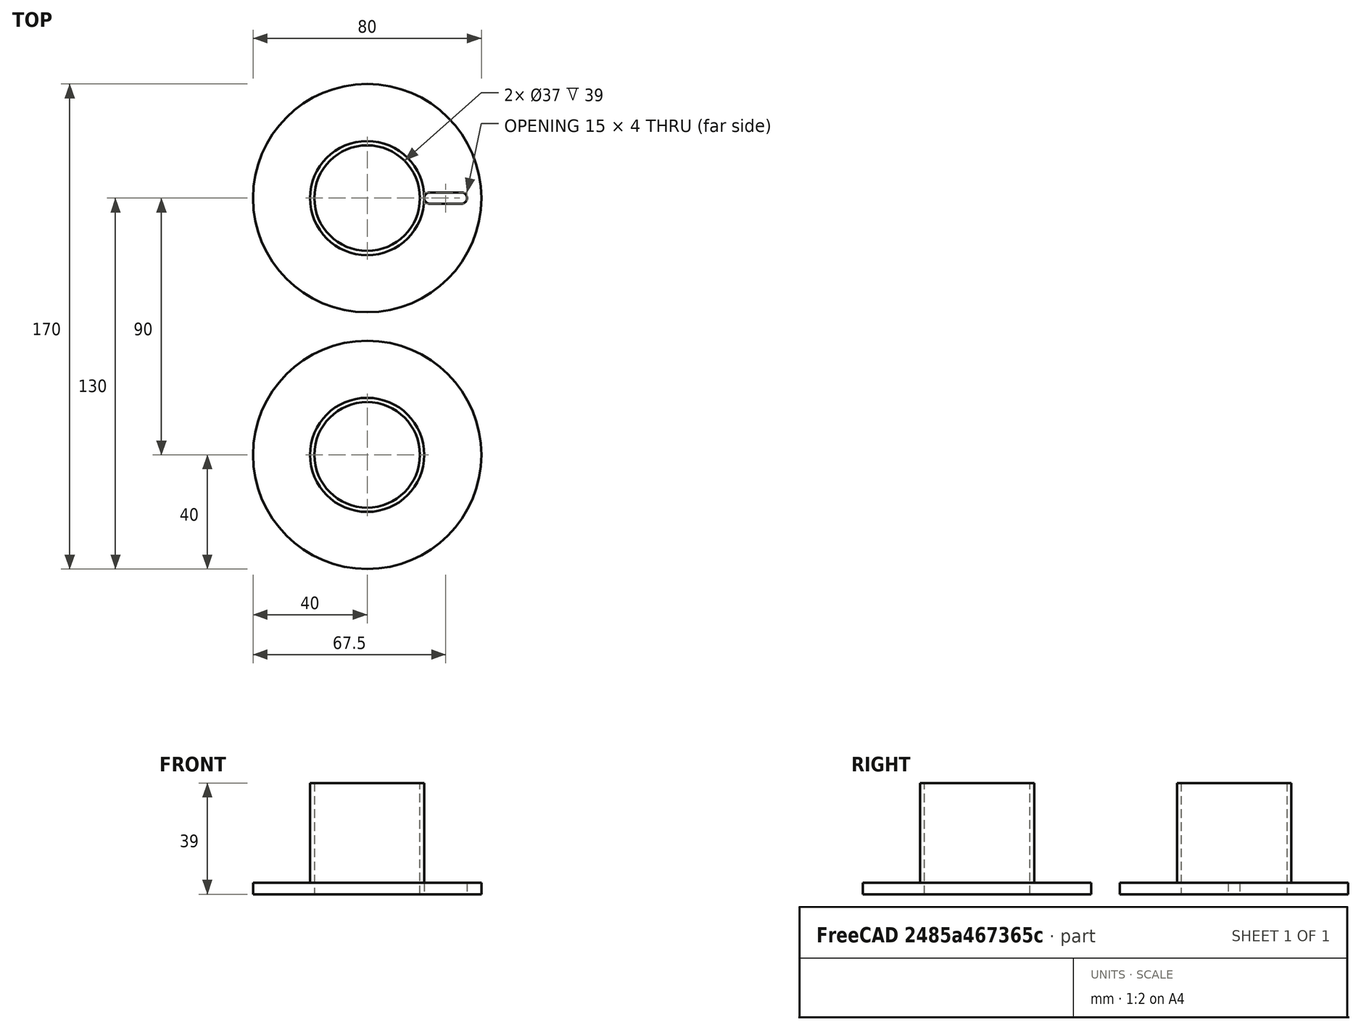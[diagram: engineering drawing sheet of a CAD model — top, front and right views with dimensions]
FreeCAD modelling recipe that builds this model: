
FCSTD DOCUMENT  (FreeCAD 0.21R33668 +26 (Git))
Label: konstra
License: All rights reserved
LicenseURL: http://en.wikipedia.org/wiki/All_rights_reserved
objects: Part::Cylinder×6, Part::Cut×6, Part::Mirroring×4, Part::Box×4, Part::MultiFuse×2, Part::Fillet×2, Spreadsheet::Sheet×1
note: 24 computed .brp shape members not serialized (recipe doc carries the construction recipe); baked Part::Feature solids carry a one-line shape summary decoded from their .brp

FEATURE [Spreadsheet::Sheet] Spreadsheet
  cells = A1='coil lenght; B1=70; C1='mm; A2='track dial; B2=600; C2='mm; A3='outer diam; B3=80; C3='mm; A4='outer wall thickness; B4=4; C4='mm
FEATURE [Part::Cylinder] Cylinder004  label="rack_straight001"
  Angle = 360
  AttacherType = Attacher::AttachEngine3D
  FirstAngle = 0
  Height = 100
  Placement = pos=(-53,0,0) rot=(0,1,0;1.5708rad)
  Radius = 18.5
  SecondAngle = 0
FEATURE [Part::Cylinder] Cylinder005  label="outside001"
  Angle = 360
  AttacherType = Attacher::AttachEngine3D
  FirstAngle = 0
  Height = 4
  Placement = pos=(-39,0,0) rot=(0,1,0;1.5708rad)
  Radius = 40
  SecondAngle = 0
  expr: .Placement.Base.x = -Spreadsheet.B1 / 2 - 4
  expr: Height = Spreadsheet.B4
  expr: Radius = Spreadsheet.B3 / 2
FEATURE [Part::Mirroring] Part__Mirroring003  label="Cylinder002 (Mirror #2)001"
  Base = (0,0,0)
  Normal = (0,1,0)
  Placement = pos=(0,0,0) rot=(0,0,1;3.14159rad)
  Source = -> Cylinder005
FEATURE [Part::Cylinder] Cylinder006  label="inside001"
  Angle = 360
  AttacherType = Attacher::AttachEngine3D
  FirstAngle = 0
  Height = 35
  Placement = pos=(0,0,0) rot=(0,-1,0;1.5708rad)
  Radius = 20
  SecondAngle = 0
  expr: Height = Spreadsheet.B1 / 2
FEATURE [Part::Mirroring] Part__Mirroring004  label="Cylinder001 (Mirror #1)001"
  Base = (0,0,0)
  Normal = (0,1,0)
  Placement = pos=(0,0,0) rot=(0,1,0;3.14159rad)
  Source = -> Cylinder006
FEATURE [Part::MultiFuse] Fusion001  label="full_spool001"
  Shapes = -> [Part__Mirroring004,Cylinder006,Part__Mirroring003,Cylinder005]
FEATURE [Part::Cut] Cut003  label="spool_full001"
  Base = -> Fusion001
  Placement = pos=(0,-90,0) rot=(0,0,1;0rad)
  Tool = -> Cylinder004
FEATURE [Part::Box] Box002  label="Cube002"
  AttacherType = Attacher::AttachEngine3D
  Height = 15
  Length = 82
  Placement = pos=(0,-2,20) rot=(0,0,1;0rad)
  Width = 4
FEATURE [Part::Fillet] Fillet001
  Base = -> Box002
  Edges = 4 edges r=1.99: [Edge9,Edge10,Edge11,Edge12]
  Placement = pos=(0,-90,0) rot=(0,0,1;0rad)
FEATURE [Part::Cylinder] Cylinder007  label="inside002"
  Angle = 360
  AttacherType = Attacher::AttachEngine3D
  FirstAngle = 0
  Height = 35
  Placement = pos=(0,0,0) rot=(0,-1,0;1.5708rad)
  Radius = 20
  SecondAngle = 0
  expr: Height = Spreadsheet.B1 / 2
FEATURE [Part::Box] Box003  label="Cube003"
  AttacherType = Attacher::AttachEngine3D
  Height = 15
  Length = 82
  Placement = pos=(0,-2,20) rot=(0,0,1;0rad)
  Width = 4
FEATURE [Part::Cylinder] Cylinder008  label="rack_straight002"
  Angle = 360
  AttacherType = Attacher::AttachEngine3D
  FirstAngle = 0
  Height = 100
  Placement = pos=(-53,0,0) rot=(0,1,0;1.5708rad)
  Radius = 18.5
  SecondAngle = 0
FEATURE [Part::Cylinder] Cylinder009  label="outside002"
  Angle = 360
  AttacherType = Attacher::AttachEngine3D
  FirstAngle = 0
  Height = 4
  Placement = pos=(-39,0,0) rot=(0,1,0;1.5708rad)
  Radius = 40
  SecondAngle = 0
  expr: .Placement.Base.x = -Spreadsheet.B1 / 2 - 4
  expr: Height = Spreadsheet.B4
  expr: Radius = Spreadsheet.B3 / 2
FEATURE [Part::Mirroring] Part__Mirroring005  label="Cylinder002 (Mirror #2)002"
  Base = (0,0,0)
  Normal = (0,1,0)
  Placement = pos=(0,0,0) rot=(0,0,1;3.14159rad)
  Source = -> Cylinder009
FEATURE [Part::Mirroring] Part__Mirroring006  label="Cylinder001 (Mirror #1)002"
  Base = (0,0,0)
  Normal = (0,1,0)
  Placement = pos=(0,0,0) rot=(0,1,0;3.14159rad)
  Source = -> Cylinder007
FEATURE [Part::Fillet] Fillet002
  Base = -> Box003
  Edges = 4 edges r=1.99: [Edge9,Edge10,Edge11,Edge12]
  Placement = pos=(0,-90,0) rot=(0,0,1;0rad)
FEATURE [Part::MultiFuse] Fusion002  label="full_spool002"
  Shapes = -> [Part__Mirroring006,Cylinder007,Part__Mirroring005,Cylinder009]
FEATURE [Part::Cut] Cut005  label="spool_full002"
  Base = -> Fusion002
  Placement = pos=(0,-90,0) rot=(0,0,1;0rad)
  Tool = -> Cylinder008
FEATURE [Part::Cut] Cut006
  Base = -> Cut005
  Placement = pos=(0,-90,0) rot=(0,-1,0;1.5708rad)
  Tool = -> Fillet002
FEATURE [Part::Cut] Cut004
  Base = -> Cut003
  Placement = pos=(0,0,0) rot=(0,1,0;1.5708rad)
  Tool = -> Fillet001
FEATURE [Part::Box] Box004  label="Cube004"
  AttacherType = Attacher::AttachEngine3D
  Height = 1000
  Length = 899
  Placement = pos=(-72,-699,0) rot=(0,-0.999938,0.01111;0rad)
  Width = 898
FEATURE [Part::Box] Box005  label="Cube005"
  AttacherType = Attacher::AttachEngine3D
  Height = 1000
  Length = 899
  Placement = pos=(-72,-699,0) rot=(0,-0.999938,0.01111;0rad)
  Width = 898
FEATURE [Part::Cut] Cut007  label="Kostra2"
  Base = -> Cut004
  Tool = -> Box004
FEATURE [Part::Cut] Cut008  label="Kostra1"
  Base = -> Cut006
  Tool = -> Box005
